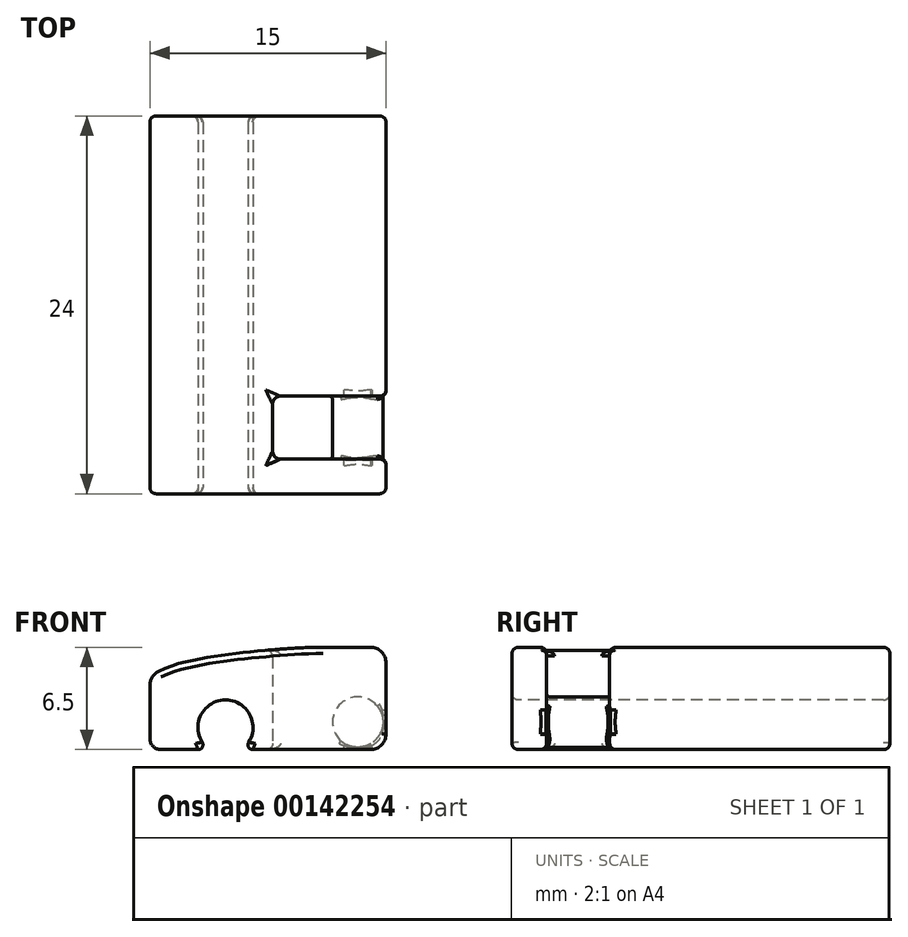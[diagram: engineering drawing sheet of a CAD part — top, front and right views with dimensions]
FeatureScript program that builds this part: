
annotation { "Feature Type Name" : "Feature", "Feature Type Description" : "" }
export const myFeature = defineFeature(function(context is Context, id is Id, definition is map)
    precondition{}
    {
        {
            var Q0;
            Q0=qCreatedBy(makeId("Front.planeOp"),FACE);
            var sketch = newSketch(context, id + "F0", { "sketchPlane" : qUnion([Q0])});
            skLineSegment(sketch, "E0", {"start": v(0, 0) * mm, "end": v(0, 4.6) * mm});
            skFitSpline(sketch, "E1", {"points": [v(0, 4.6) * mm, v(2, 5.5) * mm, v(11, 6.5) * mm], "startDerivative": vector(1.55, 1.6) * mm, "endDerivative": vector(7.91, 0) * mm});
            skLineSegment(sketch, "E2", {"start": v(11, 6.5) * mm, "end": v(15, 6.5) * mm});
            skLineSegment(sketch, "E3", {"start": v(15, 6.5) * mm, "end": v(15, 0) * mm});
            skLineSegment(sketch, "E4", {"start": v(15, 0) * mm, "end": v(0, 0) * mm});
            skSolve(sketch);
        }
        {
            var Q0;
            Q0=makeQuery(id+"F0.imprint","IMPRINT",FACE,{"disambiguationData":[TD([[makeQuery(id+"F0.imprint","IMPRINT",EDGE,{"derivedFrom":sQuery(id+"F0.wireOp",EDGE,"E0")}),-1.0]])]});
            extrude(context, id + "F1", {"entities" : qUnion([Q0]), "endBound" : BoundingType.SYMMETRIC, "depth" : 24 * mm});
        }
        {
            var Q0;
            Q0=makeQuery(id+"F1.opExtrude","SWEPT_EDGE",EDGE,{"disambiguationData":[OSD([sQuery(id+"F0.wireOp",EDGE,"E0"),sQuery(id+"F0.wireOp",EDGE,"E1")])]});
            fillet(context, id + "F2", {"entities" : qUnion([Q0]), "radius" : 1 * mm, "tangentPropagation" : true, "allowEdgeOverflow" : false});
        }
        {
            var Q0;
            {var subQ0=sQuery(id+"F0.wireOp",EDGE,"E3");var subQ1=sQuery(id+"F0.wireOp",EDGE,"E2");Q0=makeQuery(id+"F7.boolean.opBoolean","SPLIT",EDGE,{"disambiguationData":[TD([makeQuery(id+"F7.opExtrude","CAP_FACE",FACE,{"disambiguationData":[OSD([sQuery(id+"F6.wireOp",EDGE,"E5.bottom"),sQuery(id+"F6.wireOp",EDGE,"E5.top"),sQuery(id+"F6.wireOp",EDGE,"E5.left"),sQuery(id+"F6.wireOp",EDGE,"E5.right")])],"isStart":true})])],"derivedFrom":makeQuery(id+"F1.opExtrude","SWEPT_EDGE",EDGE,{"disambiguationData":[OSD([subQ1,subQ0])]})});}
            fillet(context, id + "F3", {"entities" : qUnion([Q0]), "radius" : 1 * mm, "tangentPropagation" : true, "allowEdgeOverflow" : false});
        }
        {
            var Q0;
            {var subQ0=sQuery(id+"F0.wireOp",EDGE,"E4");var subQ1=sQuery(id+"F0.wireOp",EDGE,"E3");Q0=makeQuery(id+"F7.boolean.opBoolean","SPLIT",EDGE,{"disambiguationData":[TD([makeQuery(id+"F7.opExtrude","CAP_FACE",FACE,{"disambiguationData":[OSD([sQuery(id+"F6.wireOp",EDGE,"E5.bottom"),sQuery(id+"F6.wireOp",EDGE,"E5.top"),sQuery(id+"F6.wireOp",EDGE,"E5.left"),sQuery(id+"F6.wireOp",EDGE,"E5.right")])],"isStart":true})])],"derivedFrom":makeQuery(id+"F1.opExtrude","SWEPT_EDGE",EDGE,{"disambiguationData":[OSD([subQ1,subQ0])]})});}
            fillet(context, id + "F4", {"entities" : qUnion([Q0]), "radius" : 1 * mm, "tangentPropagation" : true, "allowEdgeOverflow" : false});
        }
        {
            var Q0;
            Q0=qCreatedBy(makeId("Front.planeOp"),FACE);
            cPlane(context, id + "F5", {"entities" : qUnion([Q0]), "cplaneType" : CPlaneType.OFFSET, "offset" : (19.6 / 2) * mm, "width" : 150 * mm, "height" : 150 * mm});
        }
        {
            var Q0;
            Q0=qCreatedBy(id+"F5.planeOp",FACE);
            var sketch = newSketch(context, id + "F6", { "sketchPlane" : qUnion([Q0])});
            skLineSegment(sketch, "E5.bottom", {"start": v(15, 16.83) * mm, "end": v(7.8, 16.83) * mm});
            skLineSegment(sketch, "E5.top", {"start": v(15, -7) * mm, "end": v(7.8, -7) * mm});
            skLineSegment(sketch, "E5.left", {"start": v(15, 16.83) * mm, "end": v(15, -7) * mm});
            skLineSegment(sketch, "E5.right", {"start": v(7.8, 16.83) * mm, "end": v(7.8, -7) * mm});
            skSolve(sketch);
        }
        {
            var Q0;
            Q0 = qSketchRegion(id + "F6", true);
            extrude(context, id + "F7", {"entities" : qUnion([Q0]), "operationType" : NewBodyOperationType.REMOVE, "oppositeDirection" : true, "depth" : 4 * mm});
        }
        {
            var Q0;
            Q0=makeQuery(id+"F1.opExtrude","CAP_FACE",FACE,{"disambiguationData":[OSD([sQuery(id+"F0.wireOp",EDGE,"E0"),sQuery(id+"F0.wireOp",EDGE,"E1"),sQuery(id+"F0.wireOp",EDGE,"E2"),sQuery(id+"F0.wireOp",EDGE,"E3"),sQuery(id+"F0.wireOp",EDGE,"E4")])],"isStart":false});
            var sketch = newSketch(context, id + "F8", { "sketchPlane" : qUnion([Q0])});
            skCircle(sketch, "E6", {"center": v(4.8, 1.4) * mm, "radius": 1.75 * mm});
            skSolve(sketch);
        }
        {
            var Q0;
            Q0 = qSketchRegion(id + "F8", true);
            extrude(context, id + "F9", {"entities" : qUnion([Q0]), "operationType" : NewBodyOperationType.REMOVE, "endBound" : BoundingType.THROUGH_ALL, "oppositeDirection" : true, "depth" : 25 * mm});
        }
        {
            var Q0;
            Q0=makeQuery(id+"F9.boolean.opBoolean","INTERSECT",EDGE,{"disambiguationData":[OD(1.0)],"derivedFrom":[makeQuery(id+"F1.opExtrude","SWEPT_FACE",FACE,{"disambiguationData":[OSD([sQuery(id+"F0.wireOp",EDGE,"E4")])]}),makeQuery(id+"F9.opExtrude","SWEPT_FACE",FACE,{"disambiguationData":[OSD([sQuery(id+"F8.wireOp",EDGE,"E6")])]})]});
            var Q1;
            Q1=makeQuery(id+"F9.boolean.opBoolean","INTERSECT",EDGE,{"disambiguationData":[OD(0.0)],"derivedFrom":[makeQuery(id+"F1.opExtrude","SWEPT_FACE",FACE,{"disambiguationData":[OSD([sQuery(id+"F0.wireOp",EDGE,"E4")])]}),makeQuery(id+"F9.opExtrude","SWEPT_FACE",FACE,{"disambiguationData":[OSD([sQuery(id+"F8.wireOp",EDGE,"E6")])]})]});
            fillet(context, id + "F10", {"entities" : qUnion([Q0, Q1]), "radius" : 0.3 * mm, "tangentPropagation" : true, "allowEdgeOverflow" : false});
        }
        {
            var Q0;
            Q0=makeQuery(id+"F1.opExtrude","CAP_FACE",FACE,{"disambiguationData":[OSD([sQuery(id+"F0.wireOp",EDGE,"E0"),sQuery(id+"F0.wireOp",EDGE,"E1"),sQuery(id+"F0.wireOp",EDGE,"E2"),sQuery(id+"F0.wireOp",EDGE,"E3"),sQuery(id+"F0.wireOp",EDGE,"E4")])],"isStart":false});
            var sketch = newSketch(context, id + "F11", { "sketchPlane" : qUnion([Q0])});
            skCircle(sketch, "E7", {"center": v(13.2, 1.75) * mm, "radius": 1.6 * mm});
            skSolve(sketch);
        }
        {
            var Q0;
            Q0 = qSketchRegion(id + "F11", true);
            var Q1;
            Q1=makeQuery(id+"F1.opExtrude","CAP_FACE",FACE,{"disambiguationData":[OSD([sQuery(id+"F0.wireOp",EDGE,"E0"),sQuery(id+"F0.wireOp",EDGE,"E1"),sQuery(id+"F0.wireOp",EDGE,"E2"),sQuery(id+"F0.wireOp",EDGE,"E3"),sQuery(id+"F0.wireOp",EDGE,"E4")])],"isStart":true});
            extrude(context, id + "F12", {"entities" : qUnion([Q0]), "operationType" : NewBodyOperationType.ADD, "endBound" : BoundingType.UP_TO_SURFACE, "oppositeDirection" : true, "endBoundEntityFace" : qUnion([Q1]), "depth" : 25 * mm});
        }
        {
            var Q0;
            Q0=makeQuery(id+"FVqACIVBYguA7P8_1.1.F7.boolean.opBoolean","INTERSECT",EDGE,{"derivedFrom":[makeQuery(id+"F1.opExtrude","SWEPT_FACE",FACE,{"disambiguationData":[OSD([sQuery(id+"F0.wireOp",EDGE,"E1")])]}),makeQuery(id+"FVqACIVBYguA7P8_1.1.F7.opExtrude","CAP_FACE",FACE,{"disambiguationData":[OSD([sQuery(id+"F6.wireOp",EDGE,"E5.bottom"),sQuery(id+"F6.wireOp",EDGE,"E5.top"),sQuery(id+"F6.wireOp",EDGE,"E5.left"),sQuery(id+"F6.wireOp",EDGE,"E5.right")])],"isStart":true})]});
            var Q1;
            Q1=makeQuery(id+"FVqACIVBYguA7P8_1.1.F7.boolean.opBoolean","INTERSECT",EDGE,{"derivedFrom":[makeQuery(id+"F1.opExtrude","SWEPT_FACE",FACE,{"disambiguationData":[OSD([sQuery(id+"F0.wireOp",EDGE,"E1")])]}),makeQuery(id+"FVqACIVBYguA7P8_1.1.F7.opExtrude","CAP_FACE",FACE,{"disambiguationData":[OSD([sQuery(id+"F6.wireOp",EDGE,"E5.bottom"),sQuery(id+"F6.wireOp",EDGE,"E5.top"),sQuery(id+"F6.wireOp",EDGE,"E5.left"),sQuery(id+"F6.wireOp",EDGE,"E5.right")])],"isStart":false})]});
            var Q2;
            Q2=makeQuery(id+"F7.boolean.opBoolean","INTERSECT",EDGE,{"derivedFrom":[makeQuery(id+"F1.opExtrude","SWEPT_FACE",FACE,{"disambiguationData":[OSD([sQuery(id+"F0.wireOp",EDGE,"E1")])]}),makeQuery(id+"F7.opExtrude","CAP_FACE",FACE,{"disambiguationData":[OSD([sQuery(id+"F6.wireOp",EDGE,"E5.bottom"),sQuery(id+"F6.wireOp",EDGE,"E5.top"),sQuery(id+"F6.wireOp",EDGE,"E5.left"),sQuery(id+"F6.wireOp",EDGE,"E5.right")])],"isStart":false})]});
            var Q3;
            Q3=makeQuery(id+"F7.boolean.opBoolean","INTERSECT",EDGE,{"derivedFrom":[makeQuery(id+"F1.opExtrude","SWEPT_FACE",FACE,{"disambiguationData":[OSD([sQuery(id+"F0.wireOp",EDGE,"E1")])]}),makeQuery(id+"F7.opExtrude","CAP_FACE",FACE,{"disambiguationData":[OSD([sQuery(id+"F6.wireOp",EDGE,"E5.bottom"),sQuery(id+"F6.wireOp",EDGE,"E5.top"),sQuery(id+"F6.wireOp",EDGE,"E5.left"),sQuery(id+"F6.wireOp",EDGE,"E5.right")])],"isStart":true})]});
            var Q4;
            Q4=makeQuery(id+"F1.opExtrude","CAP_EDGE",EDGE,{"disambiguationData":[OSD([sQuery(id+"F0.wireOp",EDGE,"E1")])],"isStart":true});
            var Q5;
            Q5=makeQuery(id+"F1.opExtrude","CAP_EDGE",EDGE,{"disambiguationData":[OSD([sQuery(id+"F0.wireOp",EDGE,"E1")])],"isStart":false});
            var Q6;
            Q6=makeQuery(id+"F7.boolean.opBoolean","INTERSECT",EDGE,{"derivedFrom":[makeQuery(id+"F1.opExtrude","SWEPT_FACE",FACE,{"disambiguationData":[OSD([sQuery(id+"F0.wireOp",EDGE,"E1")])]}),makeQuery(id+"F7.opExtrude","SWEPT_FACE",FACE,{"disambiguationData":[OSD([sQuery(id+"F6.wireOp",EDGE,"E5.right")])]})]});
            var Q7;
            Q7=makeQuery(id+"FVqACIVBYguA7P8_1.1.F7.boolean.opBoolean","INTERSECT",EDGE,{"derivedFrom":[makeQuery(id+"F1.opExtrude","SWEPT_FACE",FACE,{"disambiguationData":[OSD([sQuery(id+"F0.wireOp",EDGE,"E1")])]}),makeQuery(id+"FVqACIVBYguA7P8_1.1.F7.opExtrude","SWEPT_FACE",FACE,{"disambiguationData":[OSD([sQuery(id+"F6.wireOp",EDGE,"E5.right")])]})]});
            var Q8;
            Q8=makeQuery(id+"FVqACIVBYguA7P8_1.1.F7.boolean.opBoolean","INTERSECT",EDGE,{"derivedFrom":[makeQuery(id+"F1.opExtrude","SWEPT_FACE",FACE,{"disambiguationData":[OSD([sQuery(id+"F0.wireOp",EDGE,"E4")])]}),makeQuery(id+"FVqACIVBYguA7P8_1.1.F7.opExtrude","SWEPT_FACE",FACE,{"disambiguationData":[OSD([sQuery(id+"F6.wireOp",EDGE,"E5.right")])]})]});
            var Q9;
            Q9=makeQuery(id+"F7.boolean.opBoolean","INTERSECT",EDGE,{"derivedFrom":[makeQuery(id+"F1.opExtrude","SWEPT_FACE",FACE,{"disambiguationData":[OSD([sQuery(id+"F0.wireOp",EDGE,"E4")])]}),makeQuery(id+"F7.opExtrude","SWEPT_FACE",FACE,{"disambiguationData":[OSD([sQuery(id+"F6.wireOp",EDGE,"E5.right")])]})]});
            fillet(context, id + "F13", {"entities" : qUnion([Q0, Q1, Q2, Q3, Q4, Q5, Q6, Q7, Q8, Q9]), "radius" : 0.4 * mm, "tangentPropagation" : true, "allowEdgeOverflow" : false});
        }
        {
            var Q0;
            Q0=makeQuery(id+"F7.boolean.opBoolean","COPY",EDGE,{"derivedFrom":makeQuery(id+"F7.opExtrude","CAP_EDGE",EDGE,{"disambiguationData":[OSD([sQuery(id+"F6.wireOp",EDGE,"E5.right")])],"isStart":false})});
            var Q1;
            Q1=makeQuery(id+"F7.boolean.opBoolean","COPY",EDGE,{"derivedFrom":makeQuery(id+"F7.opExtrude","CAP_EDGE",EDGE,{"disambiguationData":[OSD([sQuery(id+"F6.wireOp",EDGE,"E5.right")])],"isStart":true})});
            var Q2;
            Q2=makeQuery(id+"FVqACIVBYguA7P8_1.1.F7.boolean.opBoolean","COPY",EDGE,{"derivedFrom":makeQuery(id+"FVqACIVBYguA7P8_1.1.F7.opExtrude","CAP_EDGE",EDGE,{"disambiguationData":[OSD([sQuery(id+"F6.wireOp",EDGE,"E5.right")])],"isStart":true})});
            var Q3;
            Q3=makeQuery(id+"FVqACIVBYguA7P8_1.1.F7.boolean.opBoolean","COPY",EDGE,{"derivedFrom":makeQuery(id+"FVqACIVBYguA7P8_1.1.F7.opExtrude","CAP_EDGE",EDGE,{"disambiguationData":[OSD([sQuery(id+"F6.wireOp",EDGE,"E5.right")])],"isStart":false})});
            fillet(context, id + "F14", {"entities" : qUnion([Q0, Q1, Q2, Q3]), "radius" : 0.5 * mm, "tangentPropagation" : true, "allowEdgeOverflow" : false});
        }
        {
            var Q0;
            Q0=makeQuery(id+"F12.boolean.opBoolean","INTERSECT",EDGE,{"derivedFrom":[makeQuery(id+"FVqACIVBYguA7P8_1.1.F7.boolean.opBoolean","COPY",FACE,{"derivedFrom":makeQuery(id+"FVqACIVBYguA7P8_1.1.F7.opExtrude","CAP_FACE",FACE,{"disambiguationData":[OSD([sQuery(id+"F6.wireOp",EDGE,"E5.bottom"),sQuery(id+"F6.wireOp",EDGE,"E5.top"),sQuery(id+"F6.wireOp",EDGE,"E5.left"),sQuery(id+"F6.wireOp",EDGE,"E5.right")])],"isStart":true})}),makeQuery(id+"F12.opExtrude","SWEPT_FACE",FACE,{"disambiguationData":[OSD([sQuery(id+"F11.wireOp",EDGE,"E7")])]})]});
            var Q1;
            Q1=makeQuery(id+"F12.boolean.opBoolean","INTERSECT",EDGE,{"derivedFrom":[makeQuery(id+"FVqACIVBYguA7P8_1.1.F7.boolean.opBoolean","COPY",FACE,{"derivedFrom":makeQuery(id+"FVqACIVBYguA7P8_1.1.F7.opExtrude","CAP_FACE",FACE,{"disambiguationData":[OSD([sQuery(id+"F6.wireOp",EDGE,"E5.bottom"),sQuery(id+"F6.wireOp",EDGE,"E5.top"),sQuery(id+"F6.wireOp",EDGE,"E5.left"),sQuery(id+"F6.wireOp",EDGE,"E5.right")])],"isStart":false})}),makeQuery(id+"F12.opExtrude","SWEPT_FACE",FACE,{"disambiguationData":[OSD([sQuery(id+"F11.wireOp",EDGE,"E7")])]})]});
            var Q2;
            Q2=makeQuery(id+"F12.boolean.opBoolean","INTERSECT",EDGE,{"derivedFrom":[makeQuery(id+"F7.boolean.opBoolean","COPY",FACE,{"derivedFrom":makeQuery(id+"F7.opExtrude","CAP_FACE",FACE,{"disambiguationData":[OSD([sQuery(id+"F6.wireOp",EDGE,"E5.bottom"),sQuery(id+"F6.wireOp",EDGE,"E5.top"),sQuery(id+"F6.wireOp",EDGE,"E5.left"),sQuery(id+"F6.wireOp",EDGE,"E5.right")])],"isStart":false})}),makeQuery(id+"F12.opExtrude","SWEPT_FACE",FACE,{"disambiguationData":[OSD([sQuery(id+"F11.wireOp",EDGE,"E7")])]})]});
            var Q3;
            Q3=makeQuery(id+"F12.boolean.opBoolean","INTERSECT",EDGE,{"derivedFrom":[makeQuery(id+"F7.boolean.opBoolean","COPY",FACE,{"derivedFrom":makeQuery(id+"F7.opExtrude","CAP_FACE",FACE,{"disambiguationData":[OSD([sQuery(id+"F6.wireOp",EDGE,"E5.bottom"),sQuery(id+"F6.wireOp",EDGE,"E5.top"),sQuery(id+"F6.wireOp",EDGE,"E5.left"),sQuery(id+"F6.wireOp",EDGE,"E5.right")])],"isStart":true})}),makeQuery(id+"F12.opExtrude","SWEPT_FACE",FACE,{"disambiguationData":[OSD([sQuery(id+"F11.wireOp",EDGE,"E7")])]})]});
            fillet(context, id + "F15", {"entities" : qUnion([Q0, Q1, Q2, Q3]), "radius" : 0.2 * mm, "tangentPropagation" : true, "allowEdgeOverflow" : false});
        }
        {
            var Q0;
            Q0=makeQuery(id+"F1.opExtrude","SWEPT_EDGE",EDGE,{"disambiguationData":[OSD([sQuery(id+"F0.wireOp",EDGE,"E0"),sQuery(id+"F0.wireOp",EDGE,"E4")])]});
            fillet(context, id + "F16", {"entities" : qUnion([Q0]), "radius" : 0.7 * mm, "tangentPropagation" : true, "allowEdgeOverflow" : false});
        }
    });
